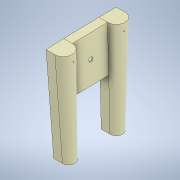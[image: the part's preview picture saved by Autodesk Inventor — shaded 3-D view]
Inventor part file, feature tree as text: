
AUTODESK INVENTOR PART (.ipt)
format: ipt  version: 2020.3 (Build 243373000, 373)  size: 210,944 bytes
history: native  units: mm
features: sketch x5, other x4, plane x3, extrude x3, shell x2, reference x2, loft x1, mirror x1, projected_geometry x1
ambient origin geometry x8: Origin, YZ Plane, XZ Plane, XY Plane, X Axis, Y Axis, Z Axis, Center Point
bodies: Solid1 (feature_tree)
feature tree (22):
  sketch  "Sketch1"  dims[d0=50.0mm d1=50.0mm d2=25.0mm]
  plane  "Work Plane2"
  loft  "Loft1"
  shell  "Shell1"  Thickness=25.0mm
  plane  "Work Plane4"
  mirror  "Mirror1"
  extrude  "Extrusion1"  Depth=35.714286mm
  shell  "Shell2"  Thickness=0.0mm
  extrude  "Extrusion2"  Depth=2.0mm
  extrude  "Extrusion3"  Depth=132.0mm
  plane  "Work Plane1"
  sketch  "Sketch2"  dims[d3=280.0mm d4=35.714286mm d5=0.0mm d6=90.0deg]
  sketch  "Sketch3"  dims[d7=0.0mm d8=90.0deg d9=2.0mm]
  projected_geometry  "Projected Loop1"
  sketch  "Sketch4"  dims[d11=50.0mm d12=132.0mm]
  sketch  "Sketch5"  dims[d13=10.0mm d14=0.0mm d15=2.0mm d16=12.0mm d17=25.0mm d18=0.0mm d19=0.0mm d20=0.0mm]
  reference  "Reference1"
  reference  "Reference2"
  other  "<userpath>\Documents\Inventor\TheArch\R&D\Alpha0\Structura\TestSpatiu.iam"
  other  "TestSpatiu.iam"
  other  "PrindereDisc:1"
  other  "PrindereDisc:2"
